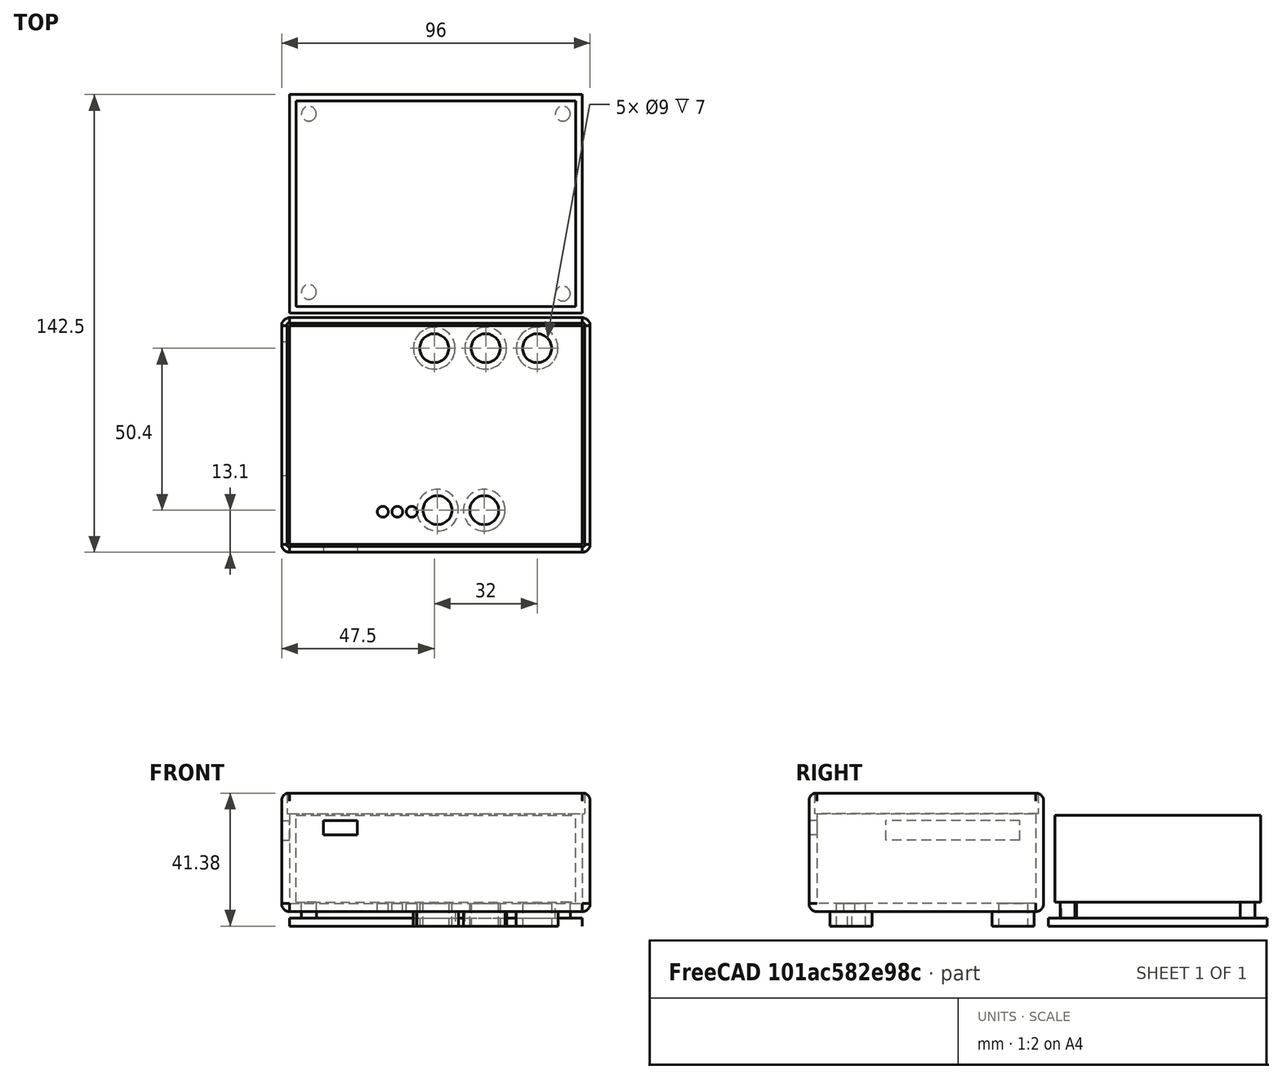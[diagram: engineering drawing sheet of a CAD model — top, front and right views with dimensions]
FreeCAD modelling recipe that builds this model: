
FCSTD DOCUMENT  (FreeCAD 0.14R3700 (Git))
Label: case-v0.2
License: CC-BY 3.0
LicenseURL: http://creativecommons.org/licenses/by/3.0/
objects: Part::Cylinder×17, Part::Box×5, Part::MultiFuse×5, Part::Cut×4, Part::FeaturePython×4, Part::Offset×1, Part::MultiCommon×1
note: 37 computed .brp shape members not serialized (recipe doc carries the construction recipe); baked Part::Feature solids carry a one-line shape summary decoded from their .brp

FEATURE [Part::Box] Box  label="board-dimensions"
  Height = 27
  Length = 87
  Placement = pos=(0,0,5) rot=(0,0,1;0rad)
  Width = 64
FEATURE [Part::Cylinder] Cylinder
  Angle = 360
  Height = 5.5
  Placement = pos=(4,4.5,-0.5) rot=(0,0,1;0rad)
  Radius = 2.3
FEATURE [Part::Cylinder] Cylinder002
  Angle = 360
  Height = 5.5
  Placement = pos=(83,60,-0.5) rot=(0,0,1;0rad)
  Radius = 2.3
FEATURE [Part::Box] Box003  label="side-pin-array-cutout"
  Height = 6.1
  Length = 10
  Placement = pos=(-6,2.9,6.1) rot=(0,0,1;0rad)
  Width = 41.64
FEATURE [Part::Box] Box004  label="usb-cutout"
  Height = 4.5
  Length = 10.6
  Placement = pos=(8.52,61,6.1) rot=(0,0,1;0rad)
  Width = 10
FEATURE [Part::Cylinder] Cylinder004
  Angle = 360
  Height = 10
  Placement = pos=(27,71,11.6) rot=(1,0,0;1.5708rad)
  Radius = 1.7
FEATURE [Part::Cylinder] Cylinder005
  Angle = 360
  Height = 10
  Placement = pos=(31.5,71,11.6) rot=(1,0,0;1.5708rad)
  Radius = 1.7
FEATURE [Part::Cylinder] Cylinder006
  Angle = 360
  Height = 10
  Placement = pos=(36,71,11.6) rot=(1,0,0;1.5708rad)
  Radius = 1.7
FEATURE [Part::MultiFuse] Fusion001  label="leds-cutout"
  Placement = pos=(0,67.5,-30) rot=(1,0,0;1.5708rad)
  Shapes = -> [Cylinder004,Cylinder005,Cylinder006]
FEATURE [Part::Cylinder] Cylinder007
  Angle = 360
  Height = 20
  Placement = pos=(44,55.4,49) rot=(1,0,0;3.14159rad)
  Radius = 4.5
FEATURE [Part::Cylinder] Cylinder008
  Angle = 360
  Height = 20
  Placement = pos=(58.55,55.4,49) rot=(1,0,0;3.14159rad)
  Radius = 4.5
FEATURE [Part::Cylinder] Cylinder009
  Angle = 360
  Height = 20
  Placement = pos=(43,5,29.6) rot=(0,0,1;0rad)
  Radius = 4.5
FEATURE [Part::Cylinder] Cylinder010
  Angle = 360
  Height = 20
  Placement = pos=(59,5,29.6) rot=(0,0,1;0rad)
  Radius = 4.5
FEATURE [Part::Cylinder] Cylinder011
  Angle = 360
  Height = 20
  Placement = pos=(75,5,29.6) rot=(0,0,1;0rad)
  Radius = 4.5
FEATURE [Part::Box] Box005  label="Cube"
  Height = 32
  Length = 91
  Placement = pos=(-2,-2,0) rot=(0,0,1;0rad)
  Width = 68
FEATURE [Part::Cylinder] Cylinder020
  Angle = 360
  Height = 7
  Placement = pos=(44,55.4,39) rot=(1,0,0;3.14159rad)
  Radius = 6.5
FEATURE [Part::Cylinder] Cylinder021
  Angle = 360
  Height = 7
  Placement = pos=(58.55,55.4,39) rot=(1,0,0;3.14159rad)
  Radius = 6.5
FEATURE [Part::Cylinder] Cylinder022
  Angle = 360
  Height = 7
  Placement = pos=(43,5,32) rot=(0,0,1;0rad)
  Radius = 6.5
FEATURE [Part::Cylinder] Cylinder023
  Angle = 360
  Height = 7
  Placement = pos=(59,5,32) rot=(0,0,1;0rad)
  Radius = 6.5
FEATURE [Part::Cylinder] Cylinder024
  Angle = 360
  Height = 7
  Placement = pos=(75,5,32) rot=(0,0,1;0rad)
  Radius = 6.5
FEATURE [Part::Offset] Offset
  Fill = false
  Intersection = false
  Join = 0
  Mode = 0
  SelfIntersection = false
  Source = -> Box005
  Value = 2.5
FEATURE [Part::MultiFuse] Fusion
  Shapes = -> [Offset,Cylinder022,Cylinder023,Cylinder024,Cylinder021,Cylinder020]
FEATURE [Part::MultiFuse] Fusion011
  Shapes = -> [Cylinder007,Cylinder008,Cylinder009,Cylinder010,Cylinder011,Box003,Fusion001,Box004]
FEATURE [Part::Cut] Cut
  Base = -> Fusion
  Tool = -> Fusion011
FEATURE [Part::FeaturePython] Clone  label="Clone of Cube"  # Draft clone (typed FeaturePython)
  Objects = -> [Box005]
  Placement = pos=(-2,-2,0) rot=(0,0,1;0rad)
  Scale = (1,1,1)
FEATURE [Part::Cut] Cut001
  Base = -> Cut
  Tool = -> Clone
FEATURE [Part::Cylinder] Cylinder025
  Angle = 360
  Height = 5.5
  Placement = pos=(4,60,-0.5) rot=(0,0,1;0rad)
  Radius = 2.3
FEATURE [Part::Cylinder] Cylinder026
  Angle = 360
  Height = 5.5
  Placement = pos=(83,4,-0.5) rot=(0,0,1;0rad)
  Radius = 2.3
FEATURE [Part::MultiFuse] Fusion012
  Shapes = -> [Cylinder025,Cylinder026,Cylinder002,Cylinder,Cut001]
FEATURE [Part::FeaturePython] Clone001  label="Clone of Cube001"  # Draft clone (typed FeaturePython)
  Objects = -> [Box005]
  Placement = pos=(-2,-2,-14) rot=(0,0,1;0rad)
  Scale = (1,1,1)
FEATURE [Part::FeaturePython] Clone002  label="Clone of Clone of Cube001"  # Draft clone (typed FeaturePython)
  Objects = -> [Clone001]
  Placement = pos=(-2,-2,-14) rot=(0,0,1;0rad)
  Scale = (1,1,1)
FEATURE [Part::Cut] Cut002  label="upper-part"
  Base = -> Fusion012
  Tool = -> Clone001
FEATURE [Part::FeaturePython] Clone003  label="Clone of Fusion012"  # Draft clone (typed FeaturePython)
  Objects = -> [Fusion012]
  Scale = (1,1,1)
FEATURE [Part::MultiCommon] Common  label="lower-part"
  Shapes = -> [Clone003,Clone002]
FEATURE [Part::Box] Box006  label="Cube001"
  Height = 32
  Length = 92.5
  Placement = pos=(-2.75,-2.75,-28) rot=(0,0,1;0rad)
  Width = 69.5
FEATURE [Part::Cut] Cut003  label="upper-part001"
  Base = -> Cut002
  Placement = pos=(0,-8,36.5) rot=(1,0,0;3.14159rad)
  Tool = -> Box006
FEATURE [Part::MultiFuse] Fusion013  label="unfolded-case"
  Shapes = -> [Common,Cut003]
